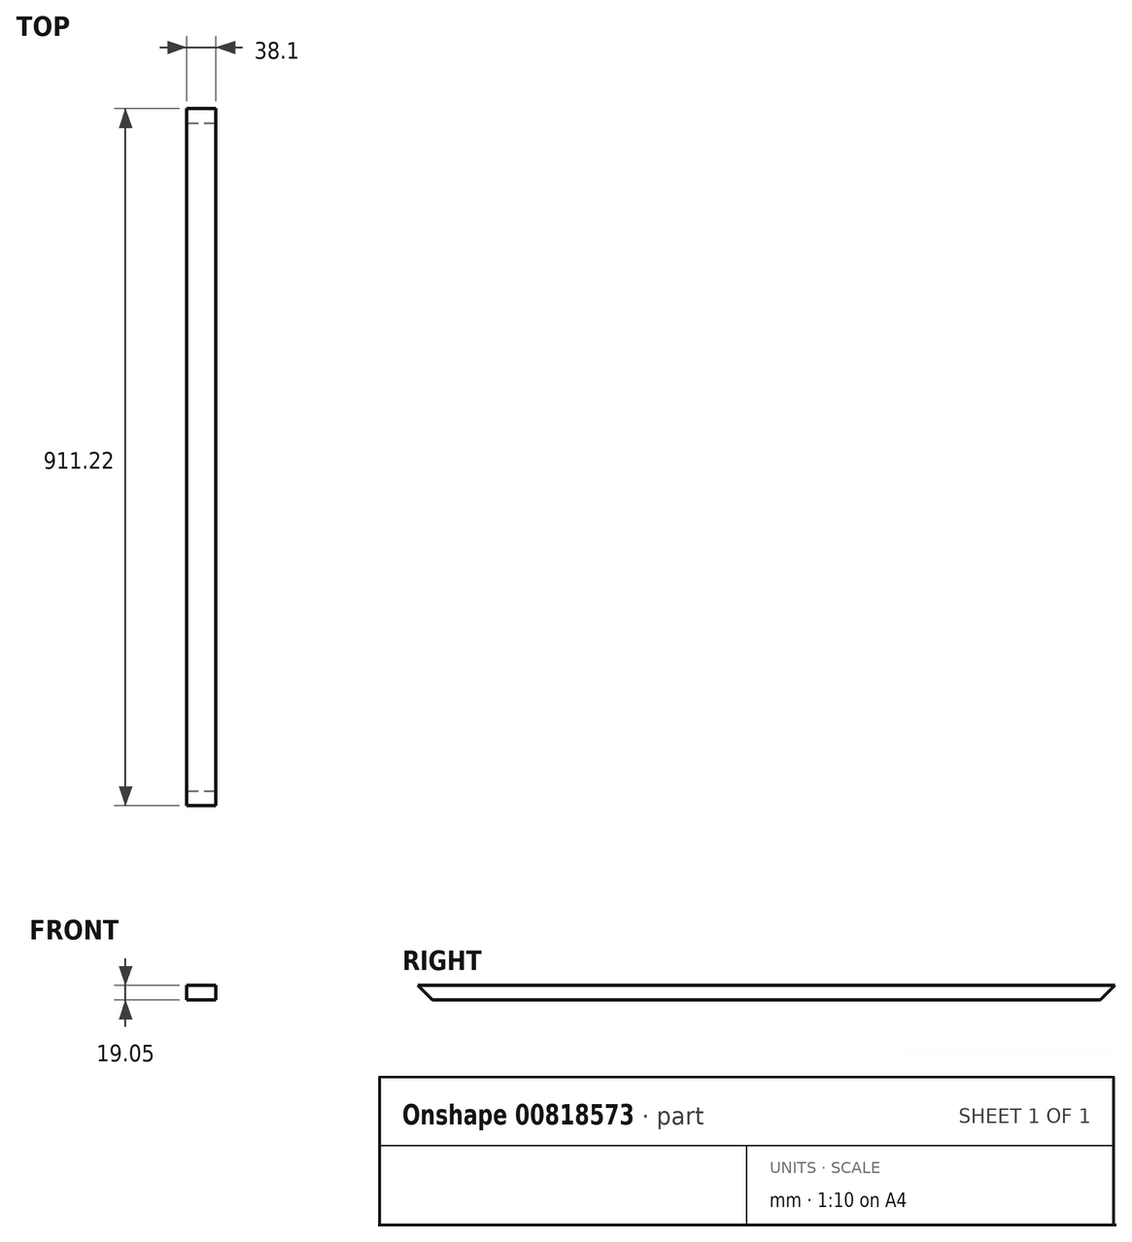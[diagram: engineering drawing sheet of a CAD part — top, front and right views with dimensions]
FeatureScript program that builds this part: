
annotation { "Feature Type Name" : "Feature", "Feature Type Description" : "" }
export const myFeature = defineFeature(function(context is Context, id is Id, definition is map)
    precondition{}
    {
        {
            var Q0;
            Q0=qCreatedBy(makeId("Front.planeOp"),FACE);
            var sketch = newSketch(context, id + "F0", { "sketchPlane" : qUnion([Q0])});
            skLineSegment(sketch, "E0.bottom", {"start": v(-12.82, 8.22) * mm, "end": v(25.28, 8.22) * mm});
            skLineSegment(sketch, "E0.top", {"start": v(-12.82, -10.83) * mm, "end": v(25.28, -10.83) * mm});
            skLineSegment(sketch, "E0.left", {"start": v(-12.82, 8.22) * mm, "end": v(-12.82, -10.83) * mm});
            skLineSegment(sketch, "E0.right", {"start": v(25.28, 8.22) * mm, "end": v(25.28, -10.83) * mm});
            skSolve(sketch);
        }
        {
            var Q0;
            Q0=qSketchRegion(id+"F0",true);
            extrude(context, id + "F1", {"entities" : qUnion([Q0]), "depth" : 911.22 * mm, "offsetDistance" : 25.4 * mm});
        }
        {
            var Q0;
            Q0=makeQuery(id+"F1.opExtrude","SWEPT_FACE",FACE,{"disambiguationData":[OSD([sQuery(id+"F0.wireOp",EDGE,"E0.right")])]});
            var sketch = newSketch(context, id + "F2", { "sketchPlane" : qUnion([Q0])});
            skLineSegment(sketch, "E1", {"start": v(-911.23, 8.22) * mm, "end": v(-892.18, -10.83) * mm});
            skLineSegment(sketch, "E2", {"start": v(-892.18, -10.83) * mm, "end": v(-911.23, -10.83) * mm});
            skLineSegment(sketch, "E3", {"start": v(-911.23, -10.83) * mm, "end": v(-911.23, 8.22) * mm});
            skLineSegment(sketch, "E4", {"start": v(0, 8.22) * mm, "end": v(-19.05, -10.83) * mm});
            skLineSegment(sketch, "E5", {"start": v(-19.05, -10.83) * mm, "end": v(0, -10.83) * mm});
            skLineSegment(sketch, "E6", {"start": v(0, -10.83) * mm, "end": v(0, 8.22) * mm});
            skSolve(sketch);
        }
        {
            var Q0;
            Q0 = qSketchRegion(id + "F2", true);
            extrude(context, id + "F3", {"entities" : qUnion([Q0]), "operationType" : NewBodyOperationType.REMOVE, "oppositeDirection" : true, "depth" : 38.1 * mm, "offsetDistance" : 25.4 * mm});
        }
    });
